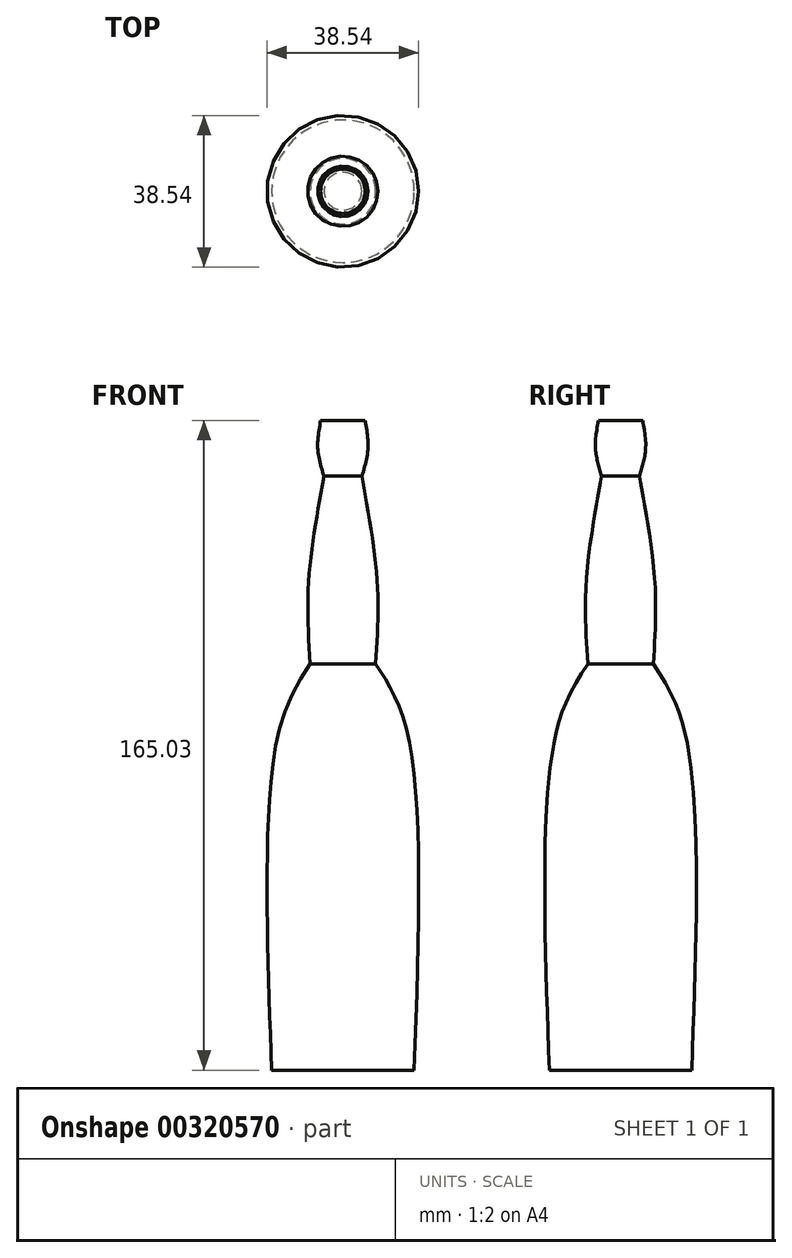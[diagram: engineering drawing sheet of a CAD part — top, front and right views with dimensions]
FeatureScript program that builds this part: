
annotation { "Feature Type Name" : "Feature", "Feature Type Description" : "" }
export const myFeature = defineFeature(function(context is Context, id is Id, definition is map)
    precondition{}
    {
        {
            var Q0;
            Q0=qCreatedBy(makeId("Front.planeOp"),FACE);
            var sketch = newSketch(context, id + "F0", { "sketchPlane" : qUnion([Q0])});
            skLineSegment(sketch, "E0", {"start": v(0, -95.27) * mm, "end": v(-13.41, -95.27) * mm});
            skFitSpline(sketch, "E1", {"points": [v(-12.24, 17.84) * mm, v(-20.45, 0) * mm, v(-22.4, -86.18) * mm], "startDerivative": vector(-29.06, -43.58) * mm, "endDerivative": vector(4.74, -151.72) * mm});
            skFitSpline(sketch, "E2", {"points": [v(-22.4, -86.18) * mm, v(-19.67, -90.87) * mm, v(-13.41, -92.05) * mm, v(-13.41, -91.66) * mm], "startDerivative": vector(3.06, -12.66) * mm, "endDerivative": vector(-1.71, 3.84) * mm});
            skLineSegment(sketch, "E3", {"start": v(-13.35, -91.8) * mm, "end": v(0, -91.8) * mm});
            skFitSpline(sketch, "E4", {"points": [v(-12.24, 17.84) * mm, v(-12.24, 38.96) * mm, v(-9.11, 65.55) * mm, v(-9.11, 65.95) * mm], "startDerivative": vector(-2.42, 40.68) * mm, "endDerivative": vector(-0.49, 3.54) * mm});
            skFitSpline(sketch, "E5", {"points": [v(-9.11, 65.55) * mm, v(-9.11, 78.07) * mm, v(9.27, 79.24) * mm, v(9.27, 65.87) * mm], "startDerivative": vector(-15.24, 46.8) * mm, "endDerivative": vector(-15.57, -50.65) * mm});
            skFitSpline(sketch, "E6", {"points": [v(-5.64, 80.02) * mm, v(-6.37, 72.98) * mm, v(-4.81, 65.87) * mm], "startDerivative": vector(-2.63, -14.16) * mm, "endDerivative": vector(4.26, -14.1) * mm});
            skFitSpline(sketch, "E7", {"points": [v(-4.81, 65.87) * mm, v(-8.72, 38.96) * mm, v(-8.33, 18.23) * mm], "startDerivative": vector(-9.5, -52) * mm, "endDerivative": vector(2.74, -43.08) * mm});
            skFitSpline(sketch, "E8", {"points": [v(-8.33, 18.23) * mm, v(-16.54, 0) * mm, v(-18.1, -85) * mm], "startDerivative": vector(-28.87, -44.34) * mm, "endDerivative": vector(5.36, -149.94) * mm});
            skPoint(sketch, "E9.1.internal.snap0", {"position": v(-6.7, -95.27) * mm});
            skFitSpline(sketch, "E9", {"points": [v(-18.1, -85) * mm, v(-6.7, -85) * mm, v(14.35, -85) * mm], "startDerivative": vector(24.85, 0) * mm, "endDerivative": vector(39.34, 0) * mm});
            skPoint(sketch, "E10.0.internal.orphan", {"position": v(15.13, 17.84) * mm});
            skPoint(sketch, "E10.1.internal.orphan", {"position": v(22.17, 0) * mm});
            skPoint(sketch, "E11.0.internal.orphan", {"position": v(15.13, -91.8) * mm});
            skPoint(sketch, "E11.1.internal.orphan", {"position": v(19.83, -91.8) * mm});
            skPoint(sketch, "E11.end.orphan", {"position": v(22.17, -85.79) * mm});
            skLineSegment(sketch, "E12.trimOffspring", {"start": v(0, -91.8) * mm, "end": v(0, -95.27) * mm, "construction": true});
            skPoint(sketch, "E13.start.orphan", {"position": v(0, 97.62) * mm});
            skLineSegment(sketch, "E14", {"start": v(0, 97.62) * mm, "end": v(0, -101.04) * mm, "construction": true});
            skLineSegment(sketch, "E15", {"start": v(0, -85) * mm, "end": v(0, -91.8) * mm});
            skLineSegment(sketch, "E16", {"start": v(-5.64, 80.02) * mm, "end": v(0, 80.02) * mm});
            skLineSegment(sketch, "E17", {"start": v(0, 80.02) * mm, "end": v(0, -85) * mm});
            skSolve(sketch);
        }
        {
            var Q0;
            Q0 = qSketchRegion(id + "F0", true);
            var Q1;
            Q1=sQuery(id+"F0.wireOp",EDGE,"E14");
            revolve(context, id + "F1", {"entities" : qUnion([Q0]), "axis" : qUnion([Q1]), "revolveType" : RevolveType.FULL});
        }
    });
